# Revit family: VRD-SMK
name_source: partatom
category: Lighting Fixtures
units: mm (PartAtom-declared; Revit-internal decimal feet)

## family parameters
Cut with Voids When Loaded = Yes
Host = Face
Light Source = Yes
Maintain Annotation Orientation = No
Part Type = Normal
Room Calculation Point = No
Round Connector Dimension = Use Diameter
Shared = No

## types (9) — shared parameters
Beam Angle = 0.00°
CRI = 90
Color Filter = 16777215
Default Elevation = 0' - 0"
Dimming Lamp Color Temperature Shift = <None>
Input Voltage = 120-277V
Lamp = LED
Load Classification = Lighting
Manufacturer = Above All Lighting
Power Factor = 0.9
Tilt Angle = 90.00°
URL = https://www.abovealllighting.com

## per-type parameters (varying)
| type | 1/2 D | Model | Photometric Web File | Wattage Comments |
| VRD-40W-4000K-SMK | 0' - 11 13/16" | VRD-4024-40901-SMK-WH | VRD-4024-40901 (1).IES | 40W |
| VRD-50W-3000K-SMK | 1' - 5 11/16" | VRD-5035-30901-SMK-WH | VRD_5035_30901.ies | 50W |
| VRD-80W-4000K-SMK | 1' - 11 19/32" | VRD-8047-40901-SMK-WH | VRD-8047-40901 (1).IES | 80W |
| VRD-100W-3000K-SMK | 2' - 5 9/16" | VRD-10059-30901-SMK-WH | VRD_10059_30901.ies | 100W |
| VRD-120W-3000K-SMK | 3' - 3 13/32" | VRD-12079-30901-SMK-WH | generic | 120W |
| VRD-160W-3000K-SMK | 4' - 1 3/16" | VRD-16098-30901-SMK-WH | generic | 160W |
| VRD-200W-3000K-SMK | 4' - 11 1/16" | VRD-200118-30901-SMK-WH | generic | 200W |
| VRD-300W-3000K-SMK | 6' - 7" | VRD-300158-30901-SMK-WH | generic | 300W |
| VRD-400W-3000K-SMK | 8' - 2 7/16" | VRD-400197-30901-SMK-WH | generic | 400W |

## geometry (parser evidence)
native form markers: Sweep x2
no freeform markers — native parametric forms only
